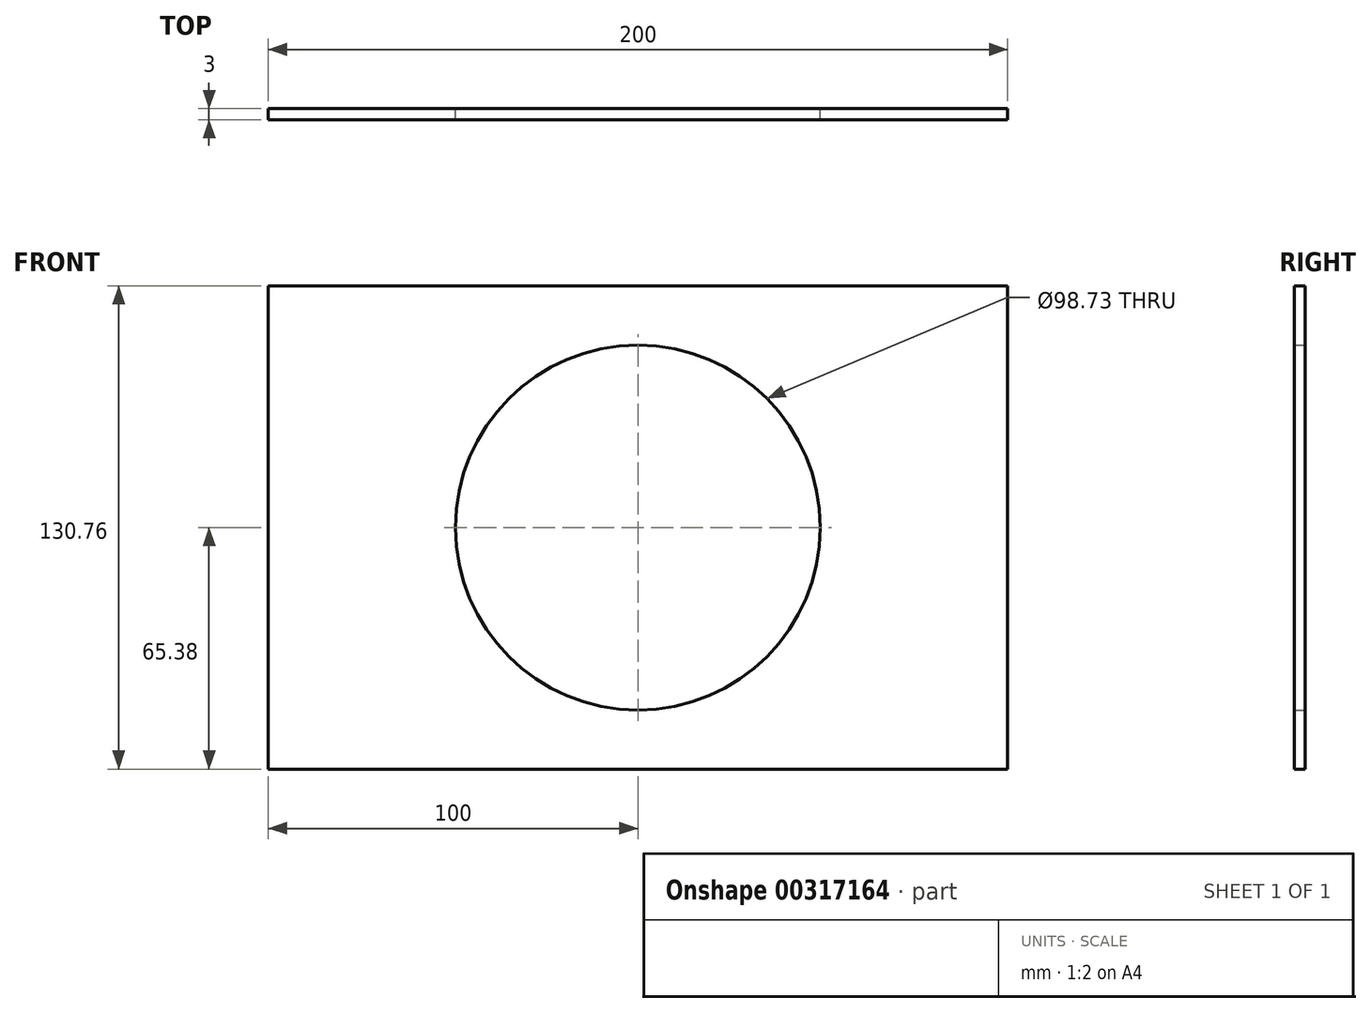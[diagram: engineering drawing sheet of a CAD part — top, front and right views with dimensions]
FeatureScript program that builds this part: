
annotation { "Feature Type Name" : "Feature", "Feature Type Description" : "" }
export const myFeature = defineFeature(function(context is Context, id is Id, definition is map)
    precondition{}
    {
        {
            var Q0;
            Q0=qCreatedBy(makeId("Front.planeOp"),FACE);
            var sketch = newSketch(context, id + "F0", { "sketchPlane" : qUnion([Q0])});
            skLineSegment(sketch, "E0.bottom", {"start": v(100, 65.38) * mm, "end": v(-100, 65.38) * mm});
            skLineSegment(sketch, "E0.top", {"start": v(100, -65.38) * mm, "end": v(-100, -65.38) * mm});
            skLineSegment(sketch, "E0.left", {"start": v(100, 65.38) * mm, "end": v(100, -65.38) * mm});
            skLineSegment(sketch, "E0.right", {"start": v(-100, 65.38) * mm, "end": v(-100, -65.38) * mm});
            skPoint(sketch, "E0.middle", {"position": v(0, 0) * mm});
            skCircle(sketch, "E1", {"center": v(0, 0) * mm, "radius": 49.37 * mm});
            skSolve(sketch);
        }
        {
            var Q0;
            Q0 = qSketchRegion(id + "F0", true);
            extrude(context, id + "F1", {"entities" : qUnion([Q0]), "depth" : 3 * mm});
        }
    });
